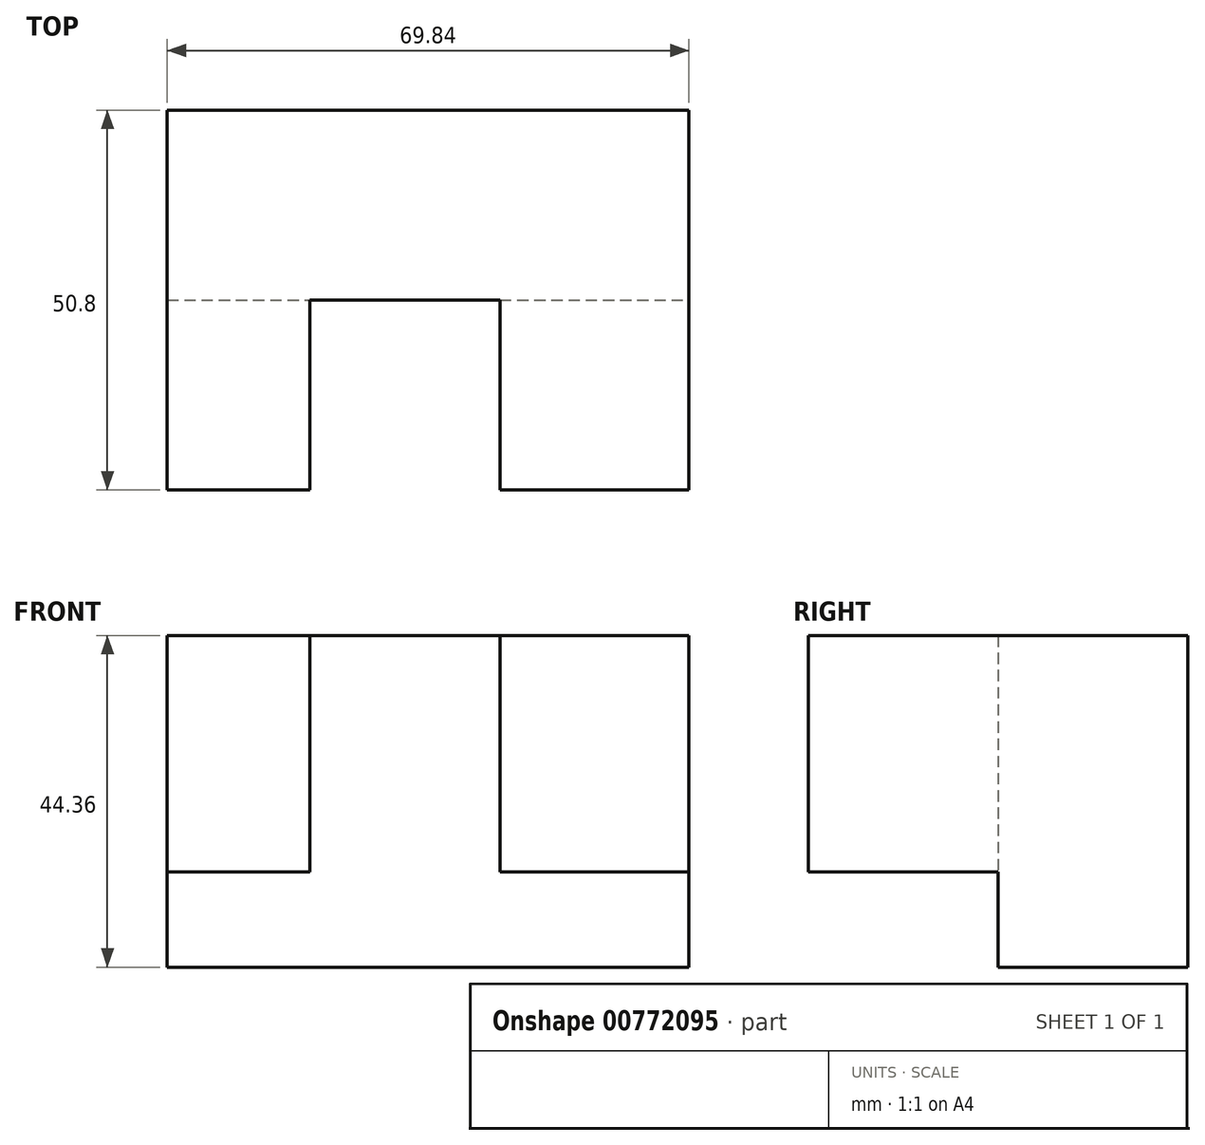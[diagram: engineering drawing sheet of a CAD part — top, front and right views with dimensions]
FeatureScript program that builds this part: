
annotation { "Feature Type Name" : "Feature", "Feature Type Description" : "" }
export const myFeature = defineFeature(function(context is Context, id is Id, definition is map)
    precondition{}
    {
        {
            var Q0;
            Q0=qCreatedBy(makeId("Front.planeOp"),FACE);
            var sketch = newSketch(context, id + "F0", { "sketchPlane" : qUnion([Q0])});
            skLineSegment(sketch, "E0", {"start": v(0, 0) * mm, "end": v(69.84, 0) * mm});
            skLineSegment(sketch, "E1", {"start": v(69.84, 0) * mm, "end": v(69.84, 44.36) * mm});
            skLineSegment(sketch, "E2", {"start": v(69.84, 44.36) * mm, "end": v(0, 44.36) * mm});
            skLineSegment(sketch, "E3", {"start": v(0, 44.36) * mm, "end": v(0, 0) * mm});
            skSolve(sketch);
        }
        {
            var Q0;
            Q0 = qSketchRegion(id + "F0", true);
            extrude(context, id + "F1", {"entities" : qUnion([Q0]), "depth" : 25.4 * mm, "offsetDistance" : 25.4 * mm});
        }
        {
            var Q0;
            Q0=makeQuery(id+"F1.opExtrude","CAP_FACE",FACE,{"disambiguationData":[OSD([sQuery(id+"F0.wireOp",EDGE,"E0"),sQuery(id+"F0.wireOp",EDGE,"E1"),sQuery(id+"F0.wireOp",EDGE,"E2"),sQuery(id+"F0.wireOp",EDGE,"E3")])],"isStart":false});
            var sketch = newSketch(context, id + "F2", { "sketchPlane" : qUnion([Q0])});
            skLineSegment(sketch, "E4", {"start": v(0, 0) * mm, "end": v(0, 12.74) * mm});
            skLineSegment(sketch, "E5", {"start": v(0, 12.74) * mm, "end": v(19.06, 12.74) * mm});
            skLineSegment(sketch, "E6", {"start": v(19.06, 12.74) * mm, "end": v(19.06, 44.36) * mm});
            skLineSegment(sketch, "E7", {"start": v(19.06, 44.36) * mm, "end": v(44.54, 44.36) * mm});
            skLineSegment(sketch, "E8", {"start": v(44.54, 44.36) * mm, "end": v(44.54, 12.74) * mm});
            skLineSegment(sketch, "E9", {"start": v(44.54, 12.74) * mm, "end": v(19.06, 12.74) * mm});
            skLineSegment(sketch, "E10", {"start": v(44.54, 12.74) * mm, "end": v(69.84, 12.74) * mm});
            skSolve(sketch);
        }
        {
            var Q0;
            {var subQ0=sQuery(id+"F2.wireOp",EDGE,"E5");Q0=makeQuery(id+"F2.imprint","IMPRINT",FACE,{"disambiguationData":[TD([[makeQuery(id+"F2.imprint","IMPRINT",EDGE,{"derivedFrom":subQ0}),1.0]])]});}
            var Q1;
            {var subQ0=sQuery(id+"F2.wireOp",EDGE,"E8");Q1=makeQuery(id+"F2.imprint","IMPRINT",FACE,{"disambiguationData":[TD([[makeQuery(id+"F2.imprint","IMPRINT",EDGE,{"derivedFrom":subQ0}),1.0]])]});}
            extrude(context, id + "F3", {"entities" : qUnion([Q0, Q1]), "operationType" : NewBodyOperationType.ADD, "depth" : 25.4 * mm, "offsetDistance" : 25.4 * mm});
        }
    });
